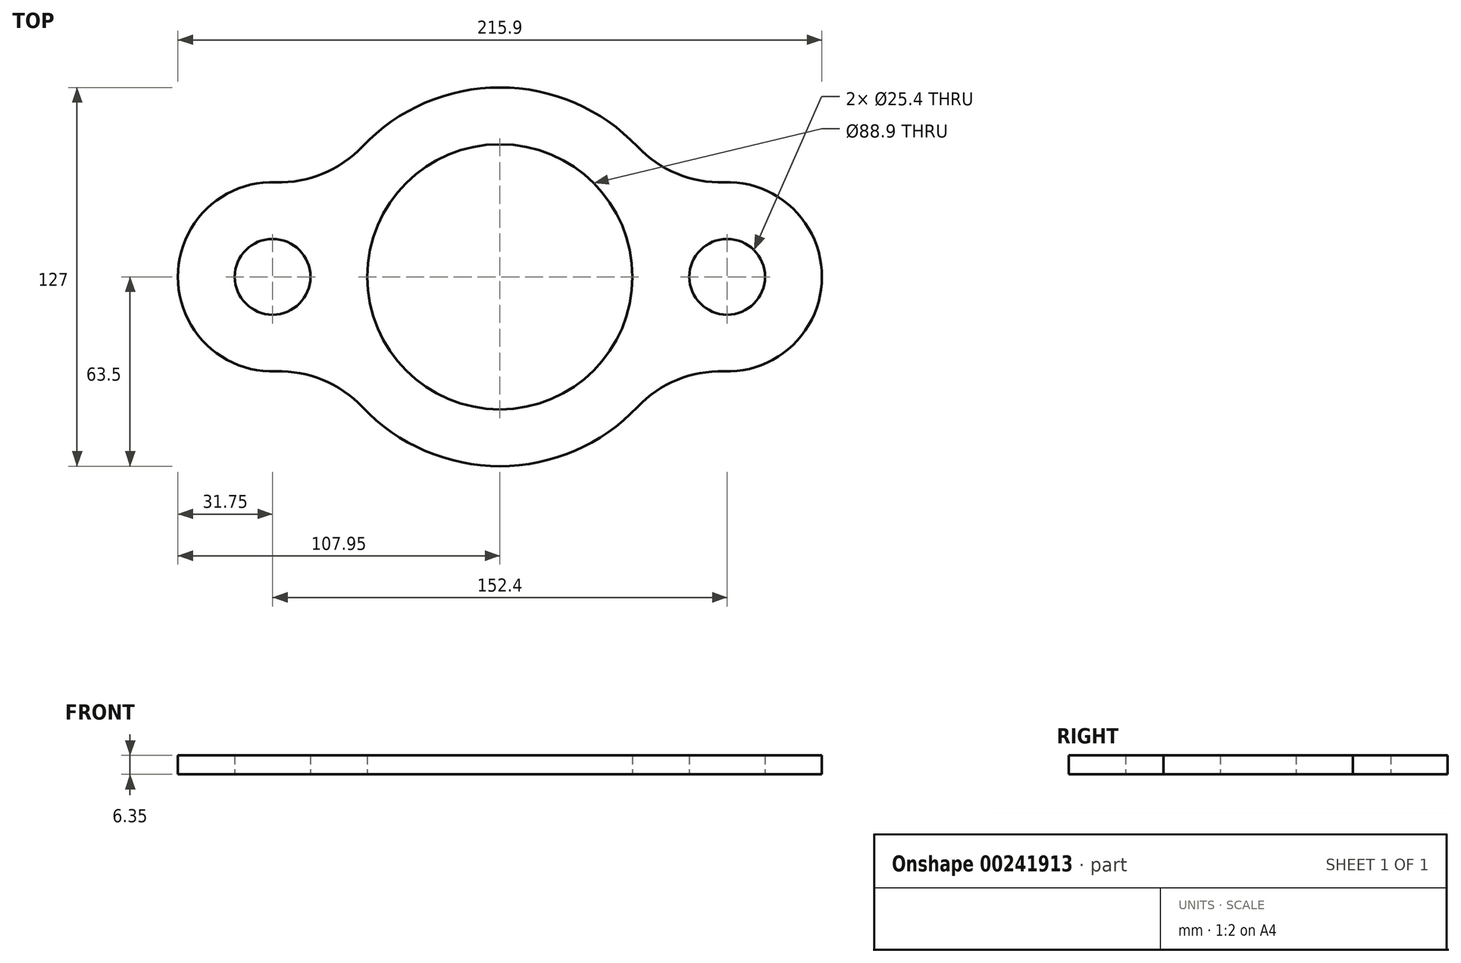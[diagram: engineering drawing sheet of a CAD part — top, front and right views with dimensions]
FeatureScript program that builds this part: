
annotation { "Feature Type Name" : "Feature", "Feature Type Description" : "" }
export const myFeature = defineFeature(function(context is Context, id is Id, definition is map)
    precondition{}
    {
        {
            var Q0;
            Q0=qCreatedBy(makeId("Top.planeOp"),FACE);
            var sketch = newSketch(context, id + "F0", { "sketchPlane" : qUnion([Q0])});
            skLineSegment(sketch, "E0", {"start": v(0, -77.97) * mm, "end": v(0, -63.5) * mm, "construction": true});
            skCircle(sketch, "E1", {"center": v(0, 0) * mm, "radius": 44.45 * mm});
            skCircle(sketch, "E2", {"center": v(-76.2, 0) * mm, "radius": 12.7 * mm});
            skCircle(sketch, "E3", {"center": v(76.2, 0) * mm, "radius": 12.7 * mm});
            skLineSegment(sketch, "E4", {"start": v(-76.2, -77.97) * mm, "end": v(-76.2, -31.75) * mm, "construction": true});
            skLineSegment(sketch, "E5", {"start": v(76.2, -77.97) * mm, "end": v(76.2, -31.75) * mm, "construction": true});
            skArc(sketch, "E6", {"start": v(-75.12, 31.73) * mm, "mid": v(-107.95, 0) * mm, "end": v(-75.12, -31.73) * mm});
            skPoint(sketch, "E7.visualSharp", {"position": v(-57.94, 25.98) * mm});
            skArc(sketch, "E7.filletArc", {"start": v(-75.12, 31.73) * mm, "mid": v(-59.35, 34.56) * mm, "end": v(-46.14, 43.63) * mm});
            skPoint(sketch, "E8.visualSharp", {"position": v(-57.94, -25.98) * mm});
            skArc(sketch, "E8.filletArc", {"start": v(-46.14, -43.63) * mm, "mid": v(-59.35, -34.56) * mm, "end": v(-75.12, -31.73) * mm});
            skArc(sketch, "E9", {"start": v(75.12, -31.73) * mm, "mid": v(107.95, 0) * mm, "end": v(75.12, 31.73) * mm});
            skArc(sketch, "E10", {"start": v(46.14, 43.63) * mm, "mid": v(0, 63.5) * mm, "end": v(-46.14, 43.63) * mm});
            skPoint(sketch, "E11.visualSharp", {"position": v(57.94, 25.98) * mm});
            skArc(sketch, "E11.filletArc", {"start": v(46.14, 43.63) * mm, "mid": v(59.35, 34.56) * mm, "end": v(75.12, 31.73) * mm});
            skPoint(sketch, "E12.visualSharp", {"position": v(57.94, -25.98) * mm});
            skArc(sketch, "E12.filletArc", {"start": v(75.12, -31.73) * mm, "mid": v(59.35, -34.56) * mm, "end": v(46.14, -43.63) * mm});
            skArc(sketch, "E13.trimOffspring", {"start": v(-46.14, -43.63) * mm, "mid": v(0, -63.5) * mm, "end": v(46.14, -43.63) * mm});
            skLineSegment(sketch, "E14.trimOffspring", {"start": v(76.2, -12.7) * mm, "end": v(76.2, 12.7) * mm, "construction": true});
            skSolve(sketch);
        }
        {
            var Q0;
            Q0 = qSketchRegion(id + "F0", true);
            extrude(context, id + "F1", {"entities" : qUnion([Q0]), "depth" : 6.35 * mm});
        }
    });
